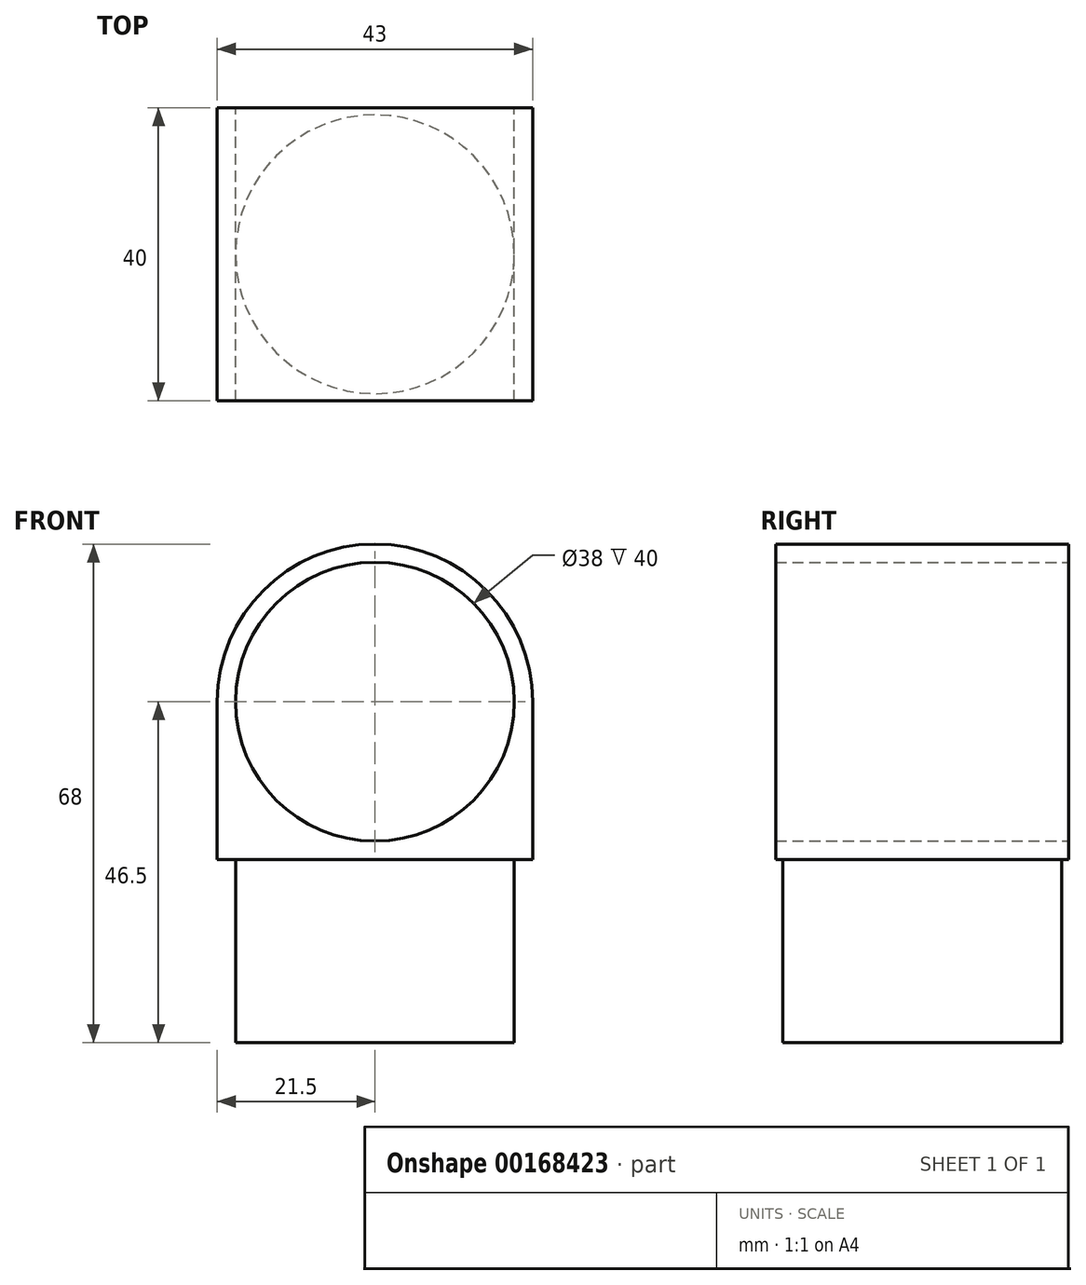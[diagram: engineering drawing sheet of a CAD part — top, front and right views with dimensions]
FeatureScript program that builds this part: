
annotation { "Feature Type Name" : "Feature", "Feature Type Description" : "" }
export const myFeature = defineFeature(function(context is Context, id is Id, definition is map)
    precondition{}
    {
        {
            var Q0;
            Q0=qCreatedBy(makeId("Front.planeOp"),FACE);
            var sketch = newSketch(context, id + "F0", { "sketchPlane" : qUnion([Q0])});
            skCircle(sketch, "E0", {"center": v(0, 21.5) * mm, "radius": 21.5 * mm});
            skCircle(sketch, "E1", {"center": v(0, 21.5) * mm, "radius": 19 * mm});
            skLineSegment(sketch, "E2", {"start": v(-21.5, 0) * mm, "end": v(-21.5, 21.5) * mm});
            skLineSegment(sketch, "E3", {"start": v(0, 21.5) * mm, "end": v(-21.5, 21.5) * mm, "construction": true});
            skLineSegment(sketch, "E4", {"start": v(-21.5, 0) * mm, "end": v(0, 0) * mm});
            skLineSegment(sketch, "E5.MirrorCS", {"start": v(0, 21.5) * mm, "end": v(21.5, 21.5) * mm, "construction": true});
            skLineSegment(sketch, "E6.MirrorCS", {"start": v(21.5, 0) * mm, "end": v(21.5, 21.5) * mm});
            skLineSegment(sketch, "E7.MirrorCS", {"start": v(21.5, 0) * mm, "end": v(0, 0) * mm});
            skSolve(sketch);
        }
        {
            var Q0;
            Q0 = qSketchRegion(id + "F0", true);
            extrude(context, id + "F1", {"entities" : qUnion([Q0]), "depth" : 40 * mm});
        }
        {
            var Q0;
            Q0=makeQuery(id+"F1.opExtrude","SWEPT_FACE",FACE,{"disambiguationData":[OSD([sQuery(id+"F0.wireOp",EDGE,"E4"),sQuery(id+"F0.wireOp",EDGE,"E7.MirrorCS")])]});
            var sketch = newSketch(context, id + "F2", { "sketchPlane" : qUnion([Q0])});
            skCircle(sketch, "E8", {"center": v(0, 20) * mm, "radius": 19 * mm});
            skPoint(sketch, "E8.centerSnap0", {"position": v(21.5, 20) * mm});
            skSolve(sketch);
        }
        {
            var Q0;
            Q0=makeQuery(id+"F2.imprint","IMPRINT",FACE,{"disambiguationData":[TD([[makeQuery(id+"F2.imprint","IMPRINT",EDGE,{"derivedFrom":sQuery(id+"F2.wireOp",EDGE,"E8")}),1.0]])]});
            extrude(context, id + "F3", {"entities" : qUnion([Q0]), "operationType" : NewBodyOperationType.ADD, "depth" : 25 * mm});
        }
    });
